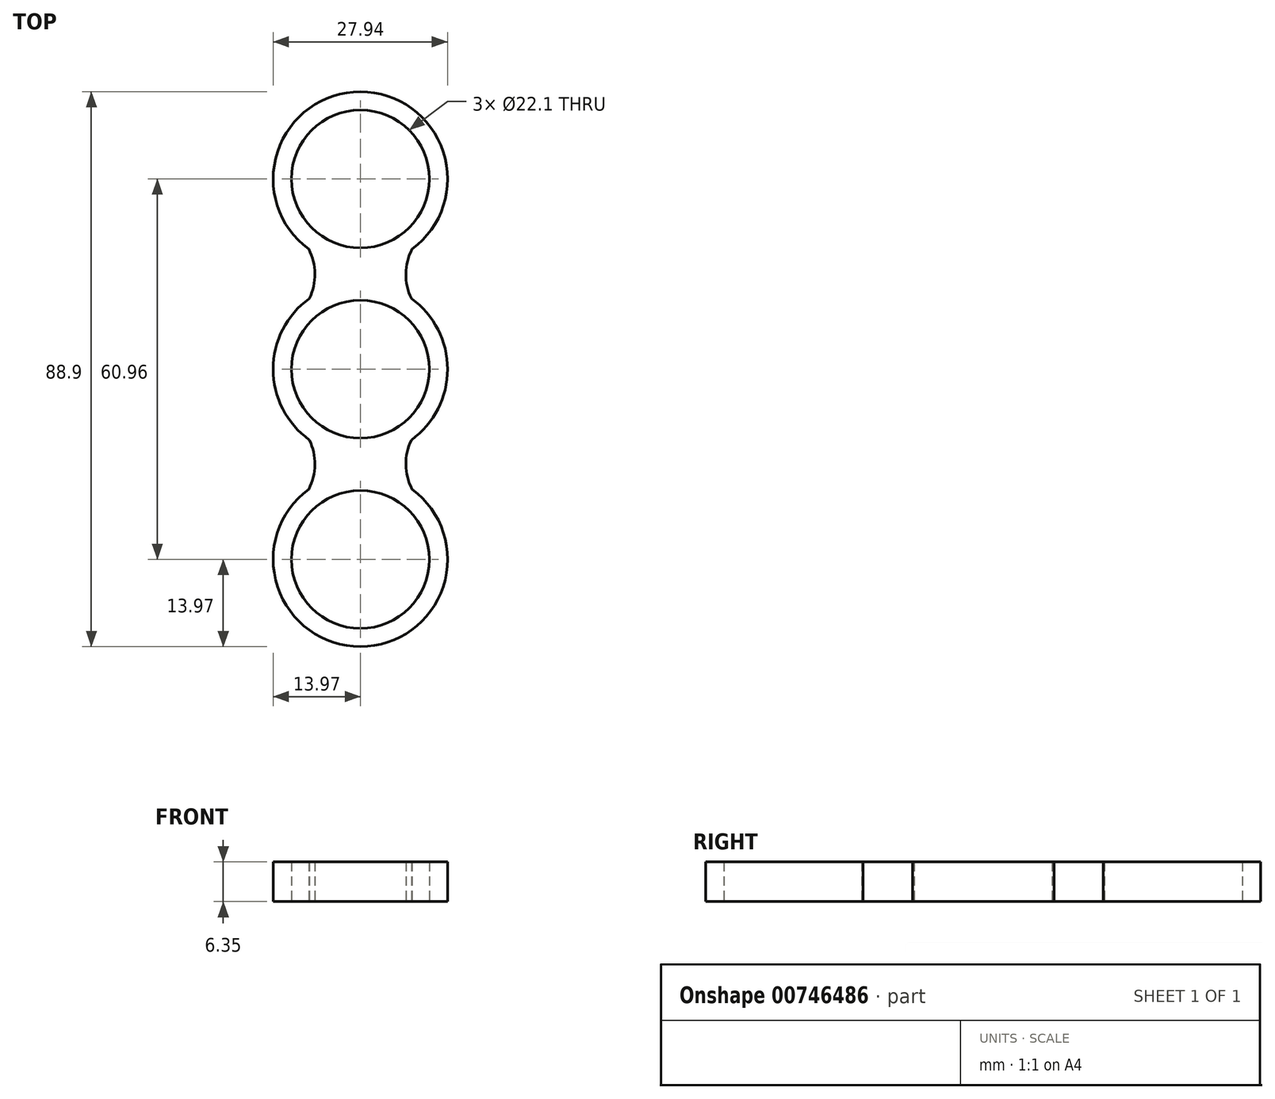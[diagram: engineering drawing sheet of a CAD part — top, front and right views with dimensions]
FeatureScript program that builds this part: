
annotation { "Feature Type Name" : "Feature", "Feature Type Description" : "" }
export const myFeature = defineFeature(function(context is Context, id is Id, definition is map)
    precondition{}
    {
        {
            var Q0;
            Q0=qCreatedBy(makeId("Top.planeOp"),FACE);
            var sketch = newSketch(context, id + "F0", { "sketchPlane" : qUnion([Q0])});
            skCircle(sketch, "E0", {"center": v(0, 0) * mm, "radius": 11.05 * mm});
            skArc(sketch, "E1", {"start": v(-8.17, 11.33) * mm, "mid": v(-13.97, 0) * mm, "end": v(-8.17, -11.33) * mm});
            skCircle(sketch, "E2", {"center": v(0, 30.48) * mm, "radius": 11.05 * mm});
            skArc(sketch, "E3", {"start": v(8.27, 19.22) * mm, "mid": v(0, 44.45) * mm, "end": v(-8.27, 19.22) * mm});
            skArc(sketch, "E4.MirrorC", {"start": v(8.27, -19.22) * mm, "mid": v(0, -44.45) * mm, "end": v(-8.27, -19.22) * mm});
            skCircle(sketch, "E5.MirrorC", {"center": v(0, -30.48) * mm, "radius": 11.05 * mm});
            skArc(sketch, "E6", {"start": v(8.27, 19.22) * mm, "mid": v(7.29, 15.29) * mm, "end": v(8.17, 11.33) * mm});
            skArc(sketch, "E7.MirrorCS", {"start": v(-8.27, 19.22) * mm, "mid": v(-7.29, 15.29) * mm, "end": v(-8.17, 11.33) * mm});
            skArc(sketch, "E8.MirrorCS", {"start": v(-8.27, -19.22) * mm, "mid": v(-7.29, -15.29) * mm, "end": v(-8.17, -11.33) * mm});
            skArc(sketch, "E9.MirrorCS", {"start": v(8.27, -19.22) * mm, "mid": v(7.29, -15.29) * mm, "end": v(8.17, -11.33) * mm});
            skArc(sketch, "E10.trimOffspring", {"start": v(8.17, -11.33) * mm, "mid": v(13.97, 0) * mm, "end": v(8.17, 11.33) * mm});
            skSolve(sketch);
        }
        {
            var Q0;
            Q0 = qSketchRegion(id + "F0", true);
            extrude(context, id + "F1", {"entities" : qUnion([Q0]), "depth" : 6.35 * mm, "offsetDistance" : 25.4 * mm});
        }
    });
